# Revit family: Toilet_Roll_Holder-Double-Bobrick-Fino-B-9547
name_source: partatom
category: Specialty Equipment
revit_build: Autodesk Revit 2018 (Build: 20170223_1515(x64)
units: mm (PartAtom-declared; Revit-internal decimal feet)

## family parameters
Cut with Voids When Loaded = No
Host = Face
OmniClass Number = 23.40.20.21
OmniClass Title = Toilet and Bath Specialties
Part Type = Normal
Room Calculation Point = No
Round Connector Dimension = Use Diameter
Shared = Yes

## types (1)
- B-9547
    Assembly Code = C1030200
    Default Elevation = 0"
    Description = Fino Collection Double Toilet Roll Holder
    Dispenser Bar Diameter = 5/8"
    Dispenser Bar Length = 10 1/2"
    Finish = Stainless_Steel-Bobrick-Type_303-Satin_Finish
    Flange Cover Diameter = 1 5/16"
    Flange Cover Radius = 21/32"
    Flange Cover Thickness Total = 1/4"
    Installation Type = Wall Mounted
    Length Of Post From Wall = 2 15/16"
    Manufacturer = Bobrick
    Material = Stainless_Steel-Bobrick-Type_303-Satin_Finish
    Model = B-9547
    Mounting Height From Floor = 26"
    Post Diameter = 3/4"
    Price = Prices may vary. Please consult Manufacturer Representative for most up-to-date price list.
    Retaining Disc Diameter = 1 1/4"
    URL = https://www.bobrick.com

## geometry (parser evidence)
native form markers: Sweep x3
no freeform markers — native parametric forms only
